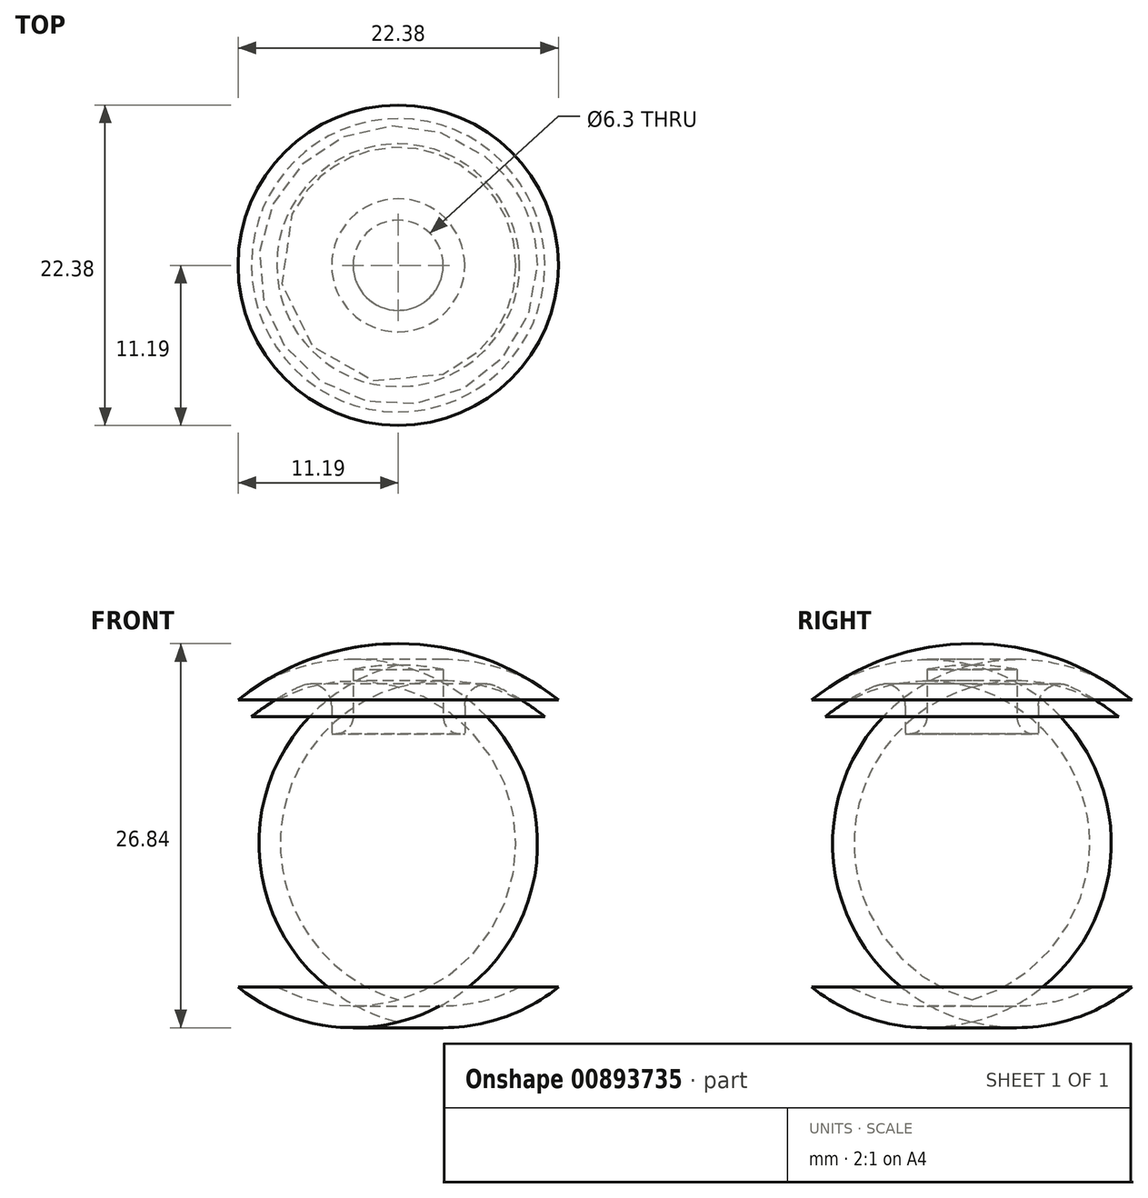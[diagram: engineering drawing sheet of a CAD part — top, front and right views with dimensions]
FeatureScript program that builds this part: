
annotation { "Feature Type Name" : "Feature", "Feature Type Description" : "" }
export const myFeature = defineFeature(function(context is Context, id is Id, definition is map)
    precondition{}
    {
        {
            var Q0;
            Q0=qCreatedBy(makeId("Front.planeOp"),FACE);
            var sketch = newSketch(context, id + "F0", { "sketchPlane" : qUnion([Q0])});
            skLineSegment(sketch, "E0", {"start": v(-4.65, 21.83) * mm, "end": v(-4.65, 17.7) * mm});
            skLineSegment(sketch, "E1", {"start": v(-4.65, 17.7) * mm, "end": v(-3.15, 17.7) * mm});
            skLineSegment(sketch, "E2", {"start": v(-3.15, 17.7) * mm, "end": v(-3.15, 22.2) * mm});
            skArc(sketch, "E3", {"start": v(0, 24) * mm, "mid": v(-5.93, 22.99) * mm, "end": v(-11.2, 20.06) * mm});
            skLineSegment(sketch, "E4", {"start": v(-16, 0) * mm, "end": v(-16, 24) * mm, "construction": true});
            skLineSegment(sketch, "E5", {"start": v(-16, 24) * mm, "end": v(0, 24) * mm, "construction": true});
            skArc(sketch, "E6", {"start": v(-11.2, 20.06) * mm, "mid": v(-16, 10.03) * mm, "end": v(-11.2, 0) * mm});
            skArc(sketch, "E7.0", {"start": v(-10.25, 18.89) * mm, "mid": v(-14.45, 8.97) * mm, "end": v(-8.48, 0) * mm});
            skArc(sketch, "E7.1", {"start": v(0, 22.5) * mm, "mid": v(-5.44, 21.57) * mm, "end": v(-10.25, 18.89) * mm});
            skLineSegment(sketch, "E8", {"start": v(-11.2, 0) * mm, "end": v(-8.48, 0) * mm});
            skLineSegment(sketch, "E9", {"start": v(0, 22.5) * mm, "end": v(0, 24) * mm});
            skLineSegment(sketch, "E10", {"start": v(-8.48, 0) * mm, "end": v(5.77, 26.72) * mm, "construction": true});
            skLineSegment(sketch, "E11", {"start": v(-10.25, 18.89) * mm, "end": v(10.05, -6.38) * mm, "construction": true});
            skSolve(sketch);
        }
        {
            var Q0;
            Q0=qSketchRegion(id+"F0",true);
            var Q1;
            Q1=sQuery(id+"F0.wireOp",EDGE,"E9");
            revolve(context, id + "F1", {"surfaceOperationType" : NewSurfaceOperationType.NEW, "entities" : qUnion([Q0]), "axis" : qUnion([Q1]), "revolveType" : RevolveType.FULL});
        }
        {
            var Q0;
            Q0=makeQuery(id+"F1.opRevolve","SWEPT_EDGE",EDGE,{"disambiguationData":[OSD([sQuery(id+"F0.wireOp",EDGE,"E1"),sQuery(id+"F0.wireOp",EDGE,"E2")])]});
            fillet(context, id + "F2", {"entities" : qUnion([Q0]), "radius" : 1.2 * mm, "tangentPropagation" : true, "allowEdgeOverflow" : false});
        }
        {
            var Q0;
            Q0=makeQuery(id+"F1.opRevolve","SWEPT_EDGE",EDGE,{"disambiguationData":[OSD([sQuery(id+"F0.wireOp",EDGE,"E0"),sQuery(id+"F0.wireOp",EDGE,"E7.1")])]});
            fillet(context, id + "F3", {"entities" : qUnion([Q0]), "radius" : 1.5 * mm, "tangentPropagation" : true, "allowEdgeOverflow" : false});
        }
    });
